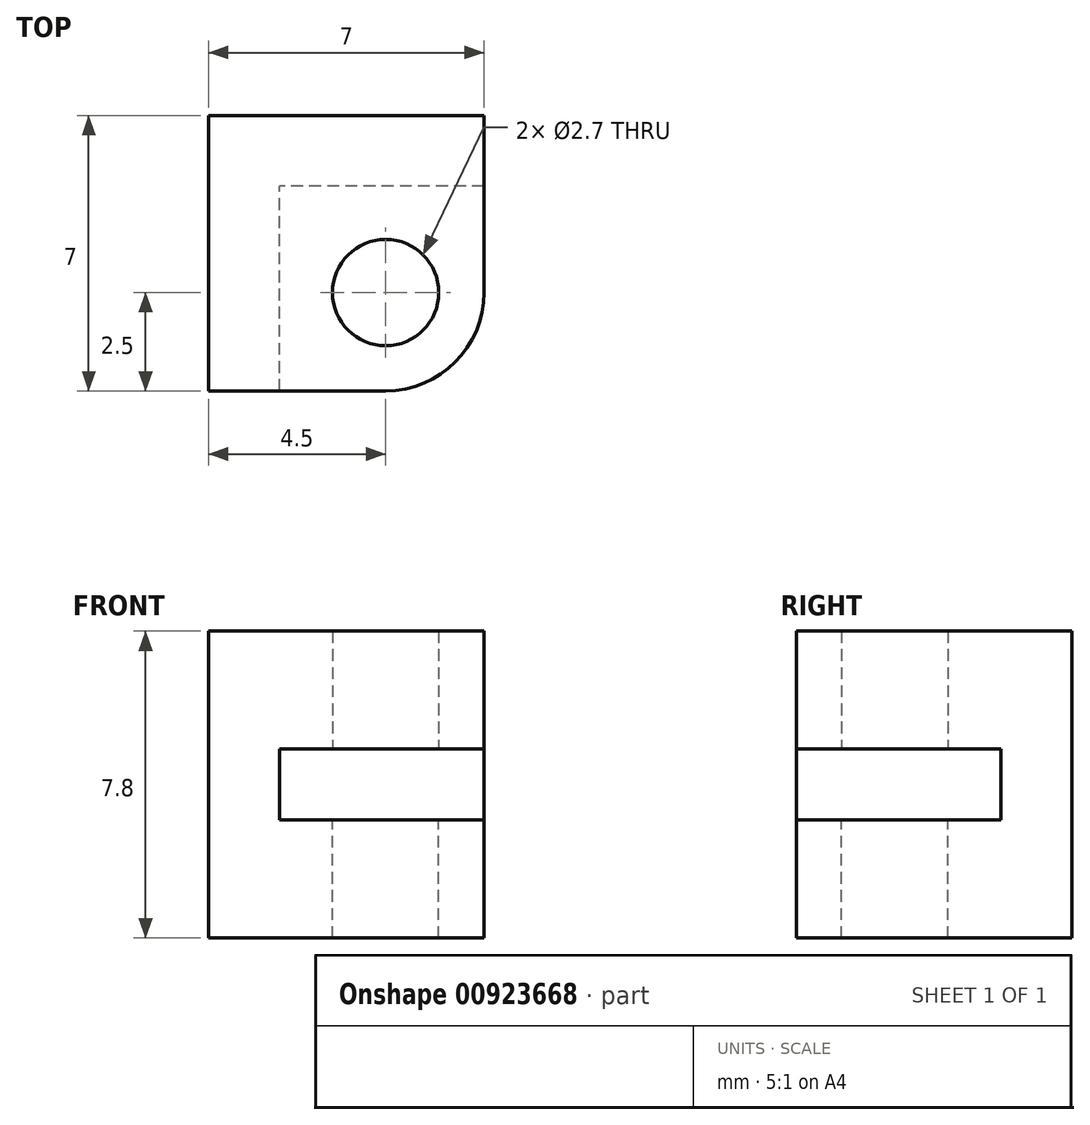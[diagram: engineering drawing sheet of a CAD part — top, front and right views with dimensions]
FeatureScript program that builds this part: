
annotation { "Feature Type Name" : "Feature", "Feature Type Description" : "" }
export const myFeature = defineFeature(function(context is Context, id is Id, definition is map)
    precondition{}
    {
        {
            var Q0;
            Q0=qCreatedBy(makeId("Top.planeOp"),FACE);
            var sketch = newSketch(context, id + "F0", { "sketchPlane" : qUnion([Q0])});
            skCircle(sketch, "E0", {"center": v(0, 0) * mm, "radius": 1.35 * mm});
            skLineSegment(sketch, "E1.bottom", {"start": v(2.5, -2.5) * mm, "end": v(-4.5, -2.5) * mm});
            skLineSegment(sketch, "E1.top", {"start": v(2.5, 4.5) * mm, "end": v(-4.5, 4.5) * mm});
            skLineSegment(sketch, "E1.left", {"start": v(2.5, -2.5) * mm, "end": v(2.5, 4.5) * mm});
            skLineSegment(sketch, "E1.right", {"start": v(-4.5, -2.5) * mm, "end": v(-4.5, 4.5) * mm});
            skPoint(sketch, "E1.middle", {"position": v(-1, 1) * mm});
            skLineSegment(sketch, "E2", {"start": v(-2.7, -2.5) * mm, "end": v(-2.7, 4.5) * mm});
            skLineSegment(sketch, "E3", {"start": v(2.5, 2.7) * mm, "end": v(-2.7, 2.7) * mm});
            skSolve(sketch);
        }
        {
            var Q0;
            {var subQ5=sQuery(id+"F0.wireOp",EDGE,"E3");Q0=makeQuery(id+"F0.imprint","IMPRINT",FACE,{"disambiguationData":[TD([[makeQuery(id+"F0.imprint","IMPRINT",EDGE,{"derivedFrom":subQ5}),-1.0]])]});}
            var Q1;
            {var subQ4=sQuery(id+"F0.wireOp",EDGE,"E1.right");Q1=makeQuery(id+"F0.imprint","IMPRINT",FACE,{"disambiguationData":[TD([[makeQuery(id+"F0.imprint","IMPRINT",EDGE,{"derivedFrom":subQ4}),-1.0]])]});}
            var Q2;
            Q2=makeQuery(id+"F0.imprint","IMPRINT",FACE,{"disambiguationData":[TD([[makeQuery(id+"F0.imprint","IMPRINT",EDGE,{"derivedFrom":sQuery(id+"F0.wireOp",EDGE,"E0")}),-1.0]])]});
            extrude(context, id + "F1", {"entities" : qUnion([Q0, Q1, Q2]), "oppositeDirection" : true, "depth" : 3 * mm, "offsetDistance" : 25 * mm});
        }
        {
            var Q0;
            Q0=makeQuery(id+"F1.opExtrude","CAP_FACE",FACE,{"disambiguationData":[OSD([sQuery(id+"F0.wireOp",EDGE,"E0"),sQuery(id+"F0.wireOp",EDGE,"E1.bottom"),sQuery(id+"F0.wireOp",EDGE,"E1.top"),sQuery(id+"F0.wireOp",EDGE,"E1.left"),sQuery(id+"F0.wireOp",EDGE,"E1.right")])],"isStart":true});
            var sketch = newSketch(context, id + "F2", { "sketchPlane" : qUnion([Q0])});
            skLineSegment(sketch, "E4.0", {"start": v(2.5, 4.5) * mm, "end": v(-4.5, 4.5) * mm});
            skLineSegment(sketch, "E5.0", {"start": v(-4.5, -2.5) * mm, "end": v(-4.5, 4.5) * mm});
            skLineSegment(sketch, "E6.0", {"start": v(2.5, -2.5) * mm, "end": v(-4.5, -2.5) * mm});
            skLineSegment(sketch, "E7.0", {"start": v(-2.7, -2.5) * mm, "end": v(-2.7, 4.5) * mm});
            skLineSegment(sketch, "E8.0", {"start": v(2.5, 2.7) * mm, "end": v(-2.7, 2.7) * mm});
            skLineSegment(sketch, "E9.0", {"start": v(2.5, -2.5) * mm, "end": v(2.5, 4.5) * mm});
            skSolve(sketch);
        }
        {
            var Q0;
            {var subQ4=sQuery(id+"F0.wireOp",EDGE,"E1.right");Q0=makeQuery(id+"F0.imprint","IMPRINT",FACE,{"disambiguationData":[TD([[makeQuery(id+"F0.imprint","IMPRINT",EDGE,{"derivedFrom":subQ4}),-1.0]])]});}
            var Q1;
            {var subQ5=sQuery(id+"F2.wireOp",EDGE,"E8.0");Q1=makeQuery(id+"F2.imprint","IMPRINT",FACE,{"disambiguationData":[TD([[makeQuery(id+"F2.imprint","IMPRINT",EDGE,{"derivedFrom":subQ5}),-1.0]])]});}
            extrude(context, id + "F3", {"entities" : qUnion([Q0, Q1]), "operationType" : NewBodyOperationType.ADD, "depth" : 1.8 * mm, "offsetDistance" : 25 * mm});
        }
        {
            var Q0;
            Q0=makeQuery(id+"F3.boolean.opBoolean","MERGE",FACE,{"derivedFrom":[makeQuery(id+"F3.opExtrude","CAP_FACE",FACE,{"disambiguationData":[OSD([sQuery(id+"F0.wireOp",EDGE,"E1.bottom"),sQuery(id+"F0.wireOp",EDGE,"E1.top"),sQuery(id+"F0.wireOp",EDGE,"E1.right"),sQuery(id+"F0.wireOp",EDGE,"E2")])],"isStart":false}),makeQuery(id+"F3.opExtrude","CAP_FACE",FACE,{"disambiguationData":[OSD([sQuery(id+"F2.wireOp",EDGE,"E4.0"),sQuery(id+"F2.wireOp",EDGE,"E7.0"),sQuery(id+"F2.wireOp",EDGE,"E8.0"),sQuery(id+"F2.wireOp",EDGE,"E9.0")])],"isStart":false})]});
            var sketch = newSketch(context, id + "F4", { "sketchPlane" : qUnion([Q0])});
            skLineSegment(sketch, "E10.0", {"start": v(2.5, 4.5) * mm, "end": v(-4.5, 4.5) * mm});
            skLineSegment(sketch, "E11.0", {"start": v(-4.5, -2.5) * mm, "end": v(-4.5, 4.5) * mm});
            skLineSegment(sketch, "E12.0", {"start": v(2.5, -2.5) * mm, "end": v(-4.5, -2.5) * mm});
            skLineSegment(sketch, "E13.0", {"start": v(2.5, -2.5) * mm, "end": v(2.5, 4.5) * mm});
            skCircle(sketch, "E14.0", {"center": v(0, 0) * mm, "radius": 1.35 * mm});
            skSolve(sketch);
        }
        {
            var Q0;
            {var subQ4=sQuery(id+"F4.wireOp",EDGE,"E10.0");Q0=makeQuery(id+"F4.imprint","IMPRINT",FACE,{"disambiguationData":[TD([[makeQuery(id+"F4.imprint","IMPRINT",EDGE,{"derivedFrom":subQ4}),1.0]])]});}
            var Q1;
            Q1=makeQuery(id+"F4.imprint","IMPRINT",FACE,{"disambiguationData":[TD([[makeQuery(id+"F4.imprint","IMPRINT",EDGE,{"derivedFrom":sQuery(id+"F4.wireOp",EDGE,"E14.0")}),-1.0]])]});
            extrude(context, id + "F5", {"entities" : qUnion([Q0, Q1]), "operationType" : NewBodyOperationType.ADD, "depth" : 3 * mm, "offsetDistance" : 25 * mm});
        }
        {
            var Q0;
            Q0=makeQuery(id+"F5.opExtrude","SWEPT_EDGE",EDGE,{"disambiguationData":[OSD([sQuery(id+"F4.wireOp",EDGE,"E12.0"),sQuery(id+"F4.wireOp",EDGE,"E13.0")])]});
            var Q1;
            Q1=makeQuery(id+"F1.opExtrude","SWEPT_EDGE",EDGE,{"disambiguationData":[OSD([sQuery(id+"F0.wireOp",EDGE,"E1.bottom"),sQuery(id+"F0.wireOp",EDGE,"E1.left")])]});
            fillet(context, id + "F6", {"entities" : qUnion([Q0, Q1]), "radius" : 2.5 * mm, "tangentPropagation" : true, "allowEdgeOverflow" : false});
        }
    });
